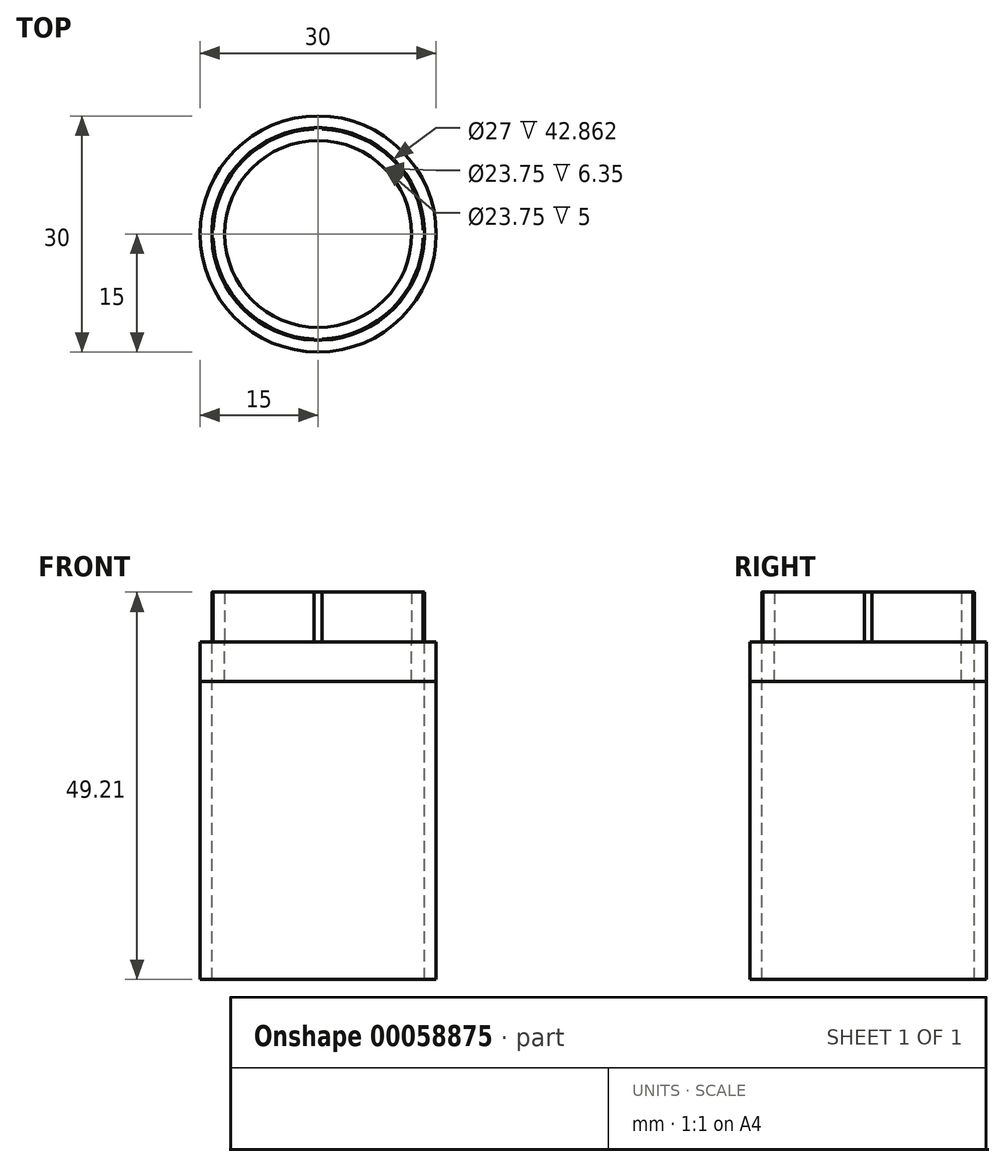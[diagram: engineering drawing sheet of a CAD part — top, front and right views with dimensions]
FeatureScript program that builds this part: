
annotation { "Feature Type Name" : "Feature", "Feature Type Description" : "" }
export const myFeature = defineFeature(function(context is Context, id is Id, definition is map)
    precondition{}
    {
        {
            var Q0;
            Q0=qCreatedBy(makeId("Top.planeOp"),FACE);
            var sketch = newSketch(context, id + "F0", { "sketchPlane" : qUnion([Q0])});
            skCircle(sketch, "E0", {"center": v(0, 0) * mm, "radius": 11.88 * mm});
            skCircle(sketch, "E1", {"center": v(0, 0) * mm, "radius": 13.35 * mm});
            skArc(sketch, "E2", {"start": v(13.5, -0.5) * mm, "mid": v(13.5, 0) * mm, "end": v(13.5, 0.5) * mm});
            skLineSegment(sketch, "E3", {"start": v(13.5, -0.5) * mm, "end": v(13.5, 0) * mm, "construction": true});
            skLineSegment(sketch, "E4", {"start": v(13.5, 0.5) * mm, "end": v(13.5, 0) * mm, "construction": true});
            skLineSegment(sketch, "E5", {"start": v(13.5, 0.5) * mm, "end": v(13.34, 0.5) * mm});
            skLineSegment(sketch, "E6", {"start": v(13.5, -0.5) * mm, "end": v(13.34, -0.5) * mm});
            skArc(sketch, "E7", {"start": v(0.5, 13.5) * mm, "mid": v(0, 13.5) * mm, "end": v(-0.5, 13.5) * mm});
            skLineSegment(sketch, "E8", {"start": v(-0.5, 13.5) * mm, "end": v(0, 13.5) * mm, "construction": true});
            skLineSegment(sketch, "E9", {"start": v(0.5, 13.5) * mm, "end": v(0, 13.5) * mm, "construction": true});
            skLineSegment(sketch, "E10", {"start": v(13.34, 0.5) * mm, "end": v(13.34, 0) * mm, "construction": true});
            skLineSegment(sketch, "E11", {"start": v(0.5, 13.5) * mm, "end": v(0.5, 13.34) * mm});
            skLineSegment(sketch, "E12", {"start": v(-0.5, 13.5) * mm, "end": v(-0.5, 13.34) * mm});
            skArc(sketch, "E13", {"start": v(-13.5, 0.5) * mm, "mid": v(-13.5, 0) * mm, "end": v(-13.5, -0.5) * mm});
            skLineSegment(sketch, "E14", {"start": v(-13.5, 0.5) * mm, "end": v(-13.5, 0) * mm, "construction": true});
            skLineSegment(sketch, "E15", {"start": v(-13.5, 0) * mm, "end": v(-13.5, -0.5) * mm, "construction": true});
            skLineSegment(sketch, "E16", {"start": v(-13.5, 0.5) * mm, "end": v(-13.34, 0.5) * mm});
            skLineSegment(sketch, "E17", {"start": v(-13.5, -0.5) * mm, "end": v(-13.34, -0.5) * mm});
            skArc(sketch, "E18", {"start": v(-0.5, -13.5) * mm, "mid": v(0, -13.5) * mm, "end": v(0.5, -13.5) * mm});
            skLineSegment(sketch, "E19", {"start": v(0.5, -13.5) * mm, "end": v(0, -13.5) * mm, "construction": true});
            skLineSegment(sketch, "E20", {"start": v(0, -13.5) * mm, "end": v(-0.5, -13.5) * mm, "construction": true});
            skLineSegment(sketch, "E21", {"start": v(0.5, -13.5) * mm, "end": v(0.5, -13.34) * mm});
            skLineSegment(sketch, "E22", {"start": v(-0.5, -13.5) * mm, "end": v(-0.5, -13.34) * mm});
            skSolve(sketch);
        }
        {
            var Q0;
            Q0=qSketchRegion(id+"F0",true);
            extrude(context, id + "F1", {"entities" : qUnion([Q0]), "depth" : 6.35 * mm});
        }
        {
            var Q0;
            Q0=qCreatedBy(makeId("Top.planeOp"),FACE);
            var sketch = newSketch(context, id + "F2", { "sketchPlane" : qUnion([Q0])});
            skCircle(sketch, "E23", {"center": v(0, 0) * mm, "radius": 13.5 * mm});
            skCircle(sketch, "E24", {"center": v(0, 0) * mm, "radius": 15 * mm});
            skSolve(sketch);
        }
        {
            var Q0;
            Q0=qSketchRegion(id+"F2",true);
            extrude(context, id + "F3", {"entities" : qUnion([Q0]), "operationType" : NewBodyOperationType.ADD, "oppositeDirection" : true, "depth" : 42.86 * mm});
        }
        {
            var Q0;
            Q0=qCreatedBy(makeId("Top.planeOp"),FACE);
            var sketch = newSketch(context, id + "F4", { "sketchPlane" : qUnion([Q0])});
            skCircle(sketch, "E25", {"center": v(0, 0) * mm, "radius": 11.88 * mm});
            skCircle(sketch, "E26", {"center": v(0, 0) * mm, "radius": 15 * mm});
            skSolve(sketch);
        }
        {
            var Q0;
            Q0=qSketchRegion(id+"F4",true);
            extrude(context, id + "F5", {"entities" : qUnion([Q0]), "oppositeDirection" : true, "depth" : 5 * mm});
        }
    });
